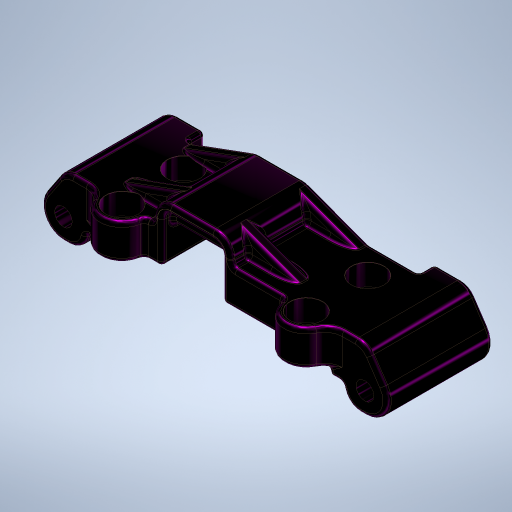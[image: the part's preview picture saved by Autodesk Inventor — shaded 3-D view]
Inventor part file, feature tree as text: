
AUTODESK INVENTOR PART (.ipt)
format: ipt  version: 2023.1 (Build 271208000, 208)  size: 1,117,696 bytes
history: native  units: in
note: dims shown in document units (in); Inventor stores cm internally (conversion verified against a paired STEP export)
features: fillet x20, sketch x14, extrude x11, projected_geometry x4, pattern_linear x2, hole x2, plane x1, rib x1
ambient origin geometry x8: Origin, YZ Plane, XZ Plane, XY Plane, X Axis, Y Axis, Z Axis, Center Point
bodies: Solid1 (feature_tree)
feature tree (55):
  extrude  "Extrusion1"  Depth=0.75in
  extrude  "Extrusion2"  Depth=1.62in
  fillet  "Fillet1"  Radius=0.315in
  extrude  "Extrusion3"  Depth=0.315in
  extrude  "Extrusion4"  Depth=0.1575in
  extrude  "Extrusion5"  Depth=0.2328in
  fillet  "Fillet2"  Radius=0.125in
  extrude  "Extrusion6"  Depth=0.25in TaperAngle=0.0deg
  extrude  "Extrusion7"  Depth=0.25in TaperAngle=0.0deg
  extrude  "Extrusion8"  Depth=0.55in
  pattern_linear  "Rectangular Pattern1"  Spacing1=0.1in  [1 undecoded]
  fillet  "Fillet3"  Radius=0.0625in
  fillet  "Fillet4"  [1 undecoded]
  fillet  "Fillet5"  [1 undecoded]
  extrude  "Extrusion9"  Depth=0.032in
  fillet  "Fillet6"  Radius=0.125in
  fillet  "Fillet7"  Radius=0.015in
  fillet  "Fillet8"  Radius=0.032in
  fillet  "Fillet9"  Radius=0.23in
  fillet  "Fillet10"  Radius=0.23in
  fillet  "Fillet11"  Radius=0.15in
  fillet  "Fillet12"  Radius=0.032in
  fillet  "Fillet13"  Radius=0.032in
  fillet  "Fillet14"  Radius=0.032in
  fillet  "Fillet15"  Radius=0.125in
  plane  "Work Plane1"
  rib  "Rib1"
  fillet  "Fillet16"  Radius=0.032in
  fillet  "Fillet17"  Radius=0.03in
  pattern_linear  "Rectangular Pattern2"  Spacing1=0.031in  [1 undecoded]
  fillet  "Fillet18"  Radius=0.031in
  hole  "Hole1"  [1 undecoded]
  hole  "Hole2"  [1 undecoded]
  extrude  "Extrusion11"  [1 undecoded]
  extrude  "Extrusion12"  Depth=0.032in
  fillet  "Fillet19"  Radius=0.1in
  fillet  "Fillet20"  Radius=0.031in
  sketch  "Sketch1"  dims[d0=0.415in d1=0.75in]
  sketch  "Sketch2"  dims[d3=0.8272in d4=1.62in d5=0.315in d6=0.0in]
  sketch  "Sketch3"  dims[d7=0.315in d8=0.315in]
  sketch  "Sketch4"  dims[d9=0.125in d10=0.0in d11=0.1575in]
  sketch  "Sketch5"  dims[d12=0.2328in d13=0.2328in d14=0.125in d15=0.0in]
  sketch  "Sketch6"  dims[d16=0.6375in d17=0.25in d18=0.0in]
  sketch  "Sketch7"  dims[d19=0.315in d20=0.25in d21=0.0in]
  sketch  "Sketch8"  dims[d22=0.125in d23=0.55in]
  sketch  "Sketch9"  dims[d24=0.415in]
  sketch  "Sketch11"  dims[d25=0.125in]
  sketch  "Sketch13"  dims[d26=0.0625in]
  sketch  "Sketch14"  dims[d27=0.25in d28=0.0in]
  sketch  "Sketch15"  dims[d29=0.4281in]
  sketch  "Sketch16"  dims[d30=0.4281in d31=0.1in d32=0.0in d33=0.0625in d34=0.0in d35=0.0in d36=0.0in d37=0.7874in d39=0.415in d40=0.125in d41=0.015in d42=0.032in d43=0.23in d44=0.23in d45=0.15in d46=0.0in d47=0.032in d48=0.032in d49=0.032in d50=0.125in d51=0.032in d52=0.03in d53=0.031in d54=0.031in d55=0.031in d56=0.031in d57=-0.125in d58=0.115in d59=0.1in d60=0.1in d61=0.0in d62=0.0in d63=0.1in d64=0.1in d65=0.031in d66=0.031in d67=0.7874in d69=0.435in d72=0.0015in d73=0.125in d74=0.75in d75=0.375in d76=0.25in d77=0.5635in d78=1.0in d79=0.8108in d80=0.125in d81=0.75in d82=0.375in d83=0.25in d84=0.5635in d85=1.0in d86=0.8108in d87=1.37in d88=0.35in d89=0.0in d90=0.1in d91=0.0in d92=0.0625in d93=0.032in]
  projected_geometry  "Project Cut Edges1"
  projected_geometry  "Project Cut Edges2"
  projected_geometry  "Project Cut Edges3"
  projected_geometry  "Project Cut Edges4"
note: 7 required parameter values undecoded (feature->parameter linkage not recoverable at this tier; creation-order binding heuristic only, values carry confidence <= 0.55)
